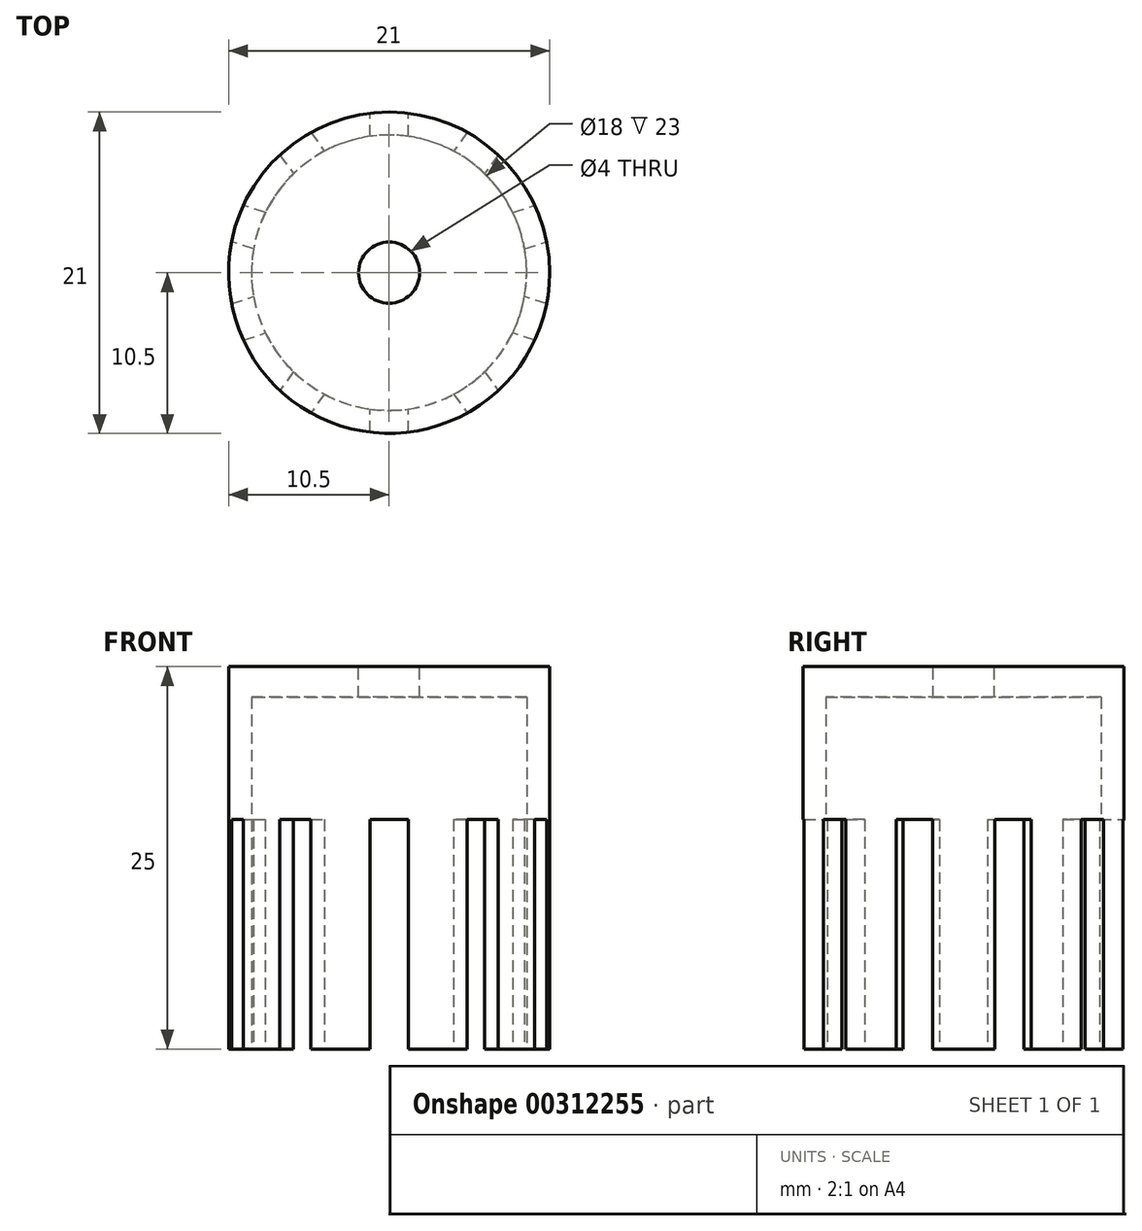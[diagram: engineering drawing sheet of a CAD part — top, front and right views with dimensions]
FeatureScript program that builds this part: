
annotation { "Feature Type Name" : "Feature", "Feature Type Description" : "" }
export const myFeature = defineFeature(function(context is Context, id is Id, definition is map)
    precondition{}
    {
        {
            var Q0;
            Q0=qCreatedBy(makeId("Top.planeOp"),FACE);
            var sketch = newSketch(context, id + "F0", { "sketchPlane" : qUnion([Q0])});
            skCircle(sketch, "E0", {"center": v(0, 0) * mm, "radius": 9 * mm});
            skCircle(sketch, "E1", {"center": v(0, 0) * mm, "radius": 10.5 * mm});
            skSolve(sketch);
        }
        {
            var Q0;
            Q0=makeQuery(id+"F0.imprint","IMPRINT",FACE,{"disambiguationData":[TD([[makeQuery(id+"F0.imprint","IMPRINT",EDGE,{"derivedFrom":sQuery(id+"F0.wireOp",EDGE,"E0")}),-1.0]])]});
            var Q1;
            Q1=makeQuery(id+"F0.imprint","IMPRINT",FACE,{"disambiguationData":[TD([[makeQuery(id+"F0.imprint","IMPRINT",EDGE,{"derivedFrom":sQuery(id+"F0.wireOp",EDGE,"E0")}),1.0]])]});
            extrude(context, id + "F1", {"entities" : qUnion([Q0, Q1]), "depth" : 25 * mm});
        }
        {
            var Q0;
            Q0=makeQuery(id+"F0.imprint","IMPRINT",FACE,{"disambiguationData":[TD([[makeQuery(id+"F0.imprint","IMPRINT",EDGE,{"derivedFrom":sQuery(id+"F0.wireOp",EDGE,"E0")}),1.0]])]});
            extrude(context, id + "F2", {"entities" : qUnion([Q0]), "operationType" : NewBodyOperationType.REMOVE, "depth" : 23 * mm});
        }
        {
            var Q0;
            Q0=makeQuery(id+"F1.opExtrude","CAP_FACE",FACE,{"disambiguationData":[OSD([sQuery(id+"F0.wireOp",EDGE,"E1")])],"isStart":false});
            var sketch = newSketch(context, id + "F3", { "sketchPlane" : qUnion([Q0])});
            skCircle(sketch, "E2", {"center": v(0, 0) * mm, "radius": 2 * mm});
            skSolve(sketch);
        }
        {
            var Q0;
            Q0=makeQuery(id+"F3.imprint","IMPRINT",FACE,{"disambiguationData":[TD([[makeQuery(id+"F3.imprint","IMPRINT",EDGE,{"derivedFrom":sQuery(id+"F3.wireOp",EDGE,"E2")}),1.0]])]});
            extrude(context, id + "F4", {"entities" : qUnion([Q0]), "operationType" : NewBodyOperationType.REMOVE, "endBound" : BoundingType.THROUGH_ALL, "oppositeDirection" : true, "depth" : 25 * mm});
        }
        {
            var Q0;
            Q0=makeQuery(id+"F0.imprint","IMPRINT",FACE,{"disambiguationData":[TD([[makeQuery(id+"F0.imprint","IMPRINT",EDGE,{"derivedFrom":sQuery(id+"F0.wireOp",EDGE,"E0")}),-1.0]])]});
            var sketch = newSketch(context, id + "F5", { "sketchPlane" : qUnion([Q0])});
            skLineSegment(sketch, "E3.bottom", {"start": v(-1.25, -16.71) * mm, "end": v(1.25, -16.71) * mm});
            skLineSegment(sketch, "E3.top", {"start": v(-1.25, 16.71) * mm, "end": v(1.25, 16.71) * mm});
            skLineSegment(sketch, "E3.left", {"start": v(-1.25, -16.71) * mm, "end": v(-1.25, 16.71) * mm});
            skLineSegment(sketch, "E3.right", {"start": v(1.25, -16.71) * mm, "end": v(1.25, 16.71) * mm});
            skLineSegment(sketch, "E4.1.0", {"start": v(15.5, -6.35) * mm, "end": v(-16.28, 3.98) * mm});
            skLineSegment(sketch, "E4.1.1", {"start": v(16.28, -3.98) * mm, "end": v(-15.5, 6.35) * mm});
            skLineSegment(sketch, "E4.1.2", {"start": v(15.5, -6.35) * mm, "end": v(16.28, -3.98) * mm});
            skLineSegment(sketch, "E4.1.3", {"start": v(-16.28, 3.98) * mm, "end": v(-15.5, 6.35) * mm});
            skLineSegment(sketch, "E4.2.0", {"start": v(10.83, 12.78) * mm, "end": v(-8.81, -14.25) * mm});
            skLineSegment(sketch, "E4.2.1", {"start": v(8.81, 14.25) * mm, "end": v(-10.83, -12.78) * mm});
            skLineSegment(sketch, "E4.2.2", {"start": v(10.83, 12.78) * mm, "end": v(8.81, 14.25) * mm});
            skLineSegment(sketch, "E4.2.3", {"start": v(-8.81, -14.25) * mm, "end": v(-10.83, -12.78) * mm});
            skLineSegment(sketch, "E4.3.0", {"start": v(-8.81, 14.25) * mm, "end": v(10.83, -12.78) * mm});
            skLineSegment(sketch, "E4.3.1", {"start": v(-10.83, 12.78) * mm, "end": v(8.81, -14.25) * mm});
            skLineSegment(sketch, "E4.3.2", {"start": v(-8.81, 14.25) * mm, "end": v(-10.83, 12.78) * mm});
            skLineSegment(sketch, "E4.3.3", {"start": v(10.83, -12.78) * mm, "end": v(8.81, -14.25) * mm});
            skLineSegment(sketch, "E4.4.0", {"start": v(-16.28, -3.98) * mm, "end": v(15.5, 6.35) * mm});
            skLineSegment(sketch, "E4.4.1", {"start": v(-15.5, -6.35) * mm, "end": v(16.28, 3.98) * mm});
            skLineSegment(sketch, "E4.4.2", {"start": v(-16.28, -3.98) * mm, "end": v(-15.5, -6.35) * mm});
            skLineSegment(sketch, "E4.4.3", {"start": v(15.5, 6.35) * mm, "end": v(16.28, 3.98) * mm});
            skPoint(sketch, "E4.center", {"position": v(0, 0) * mm});
            skSolve(sketch);
        }
        {
            var Q0;
            {var subQ0=sQuery(id+"F5.wireOp",EDGE,"E4.2.0");var subQ1=makeQuery(id+"F0.imprint","IMPRINT",EDGE,{"derivedFrom":sQuery(id+"F0.wireOp",EDGE,"E1")});var subQ2=makeQuery(id+"F5.imprint","INTERSECT",VERTEX,{"disambiguationData":[OD(0.0)],"derivedFrom":[subQ1,subQ0]});Q0=makeQuery(id+"F5.imprint","IMPRINT",FACE,{"disambiguationData":[TD([[makeQuery(id+"F5.imprint","IMPRINT",EDGE,{"disambiguationData":[TD([[subQ2,-1.0]])],"derivedFrom":subQ0}),-1.0]])]});}
            var Q1;
            {var subQ0=sQuery(id+"F5.wireOp",EDGE,"E4.4.0");var subQ1=makeQuery(id+"F0.imprint","IMPRINT",EDGE,{"derivedFrom":sQuery(id+"F0.wireOp",EDGE,"E1")});var subQ2=makeQuery(id+"F5.imprint","INTERSECT",VERTEX,{"disambiguationData":[OD(1.0)],"derivedFrom":[subQ1,subQ0]});Q1=makeQuery(id+"F5.imprint","IMPRINT",FACE,{"disambiguationData":[TD([[makeQuery(id+"F5.imprint","IMPRINT",EDGE,{"disambiguationData":[TD([[subQ2,1.0]])],"derivedFrom":subQ0}),-1.0]])]});}
            var Q2;
            {var subQ0=sQuery(id+"F5.wireOp",EDGE,"E3.left");var subQ1=makeQuery(id+"F0.imprint","IMPRINT",EDGE,{"derivedFrom":sQuery(id+"F0.wireOp",EDGE,"E1")});var subQ2=makeQuery(id+"F5.imprint","INTERSECT",VERTEX,{"disambiguationData":[OD(1.0)],"derivedFrom":[subQ1,subQ0]});Q2=makeQuery(id+"F5.imprint","IMPRINT",FACE,{"disambiguationData":[TD([[makeQuery(id+"F5.imprint","IMPRINT",EDGE,{"disambiguationData":[TD([[subQ2,1.0]])],"derivedFrom":subQ0}),-1.0]])]});}
            var Q3;
            {var subQ0=sQuery(id+"F5.wireOp",EDGE,"E4.3.0");var subQ1=makeQuery(id+"F0.imprint","IMPRINT",EDGE,{"derivedFrom":sQuery(id+"F0.wireOp",EDGE,"E1")});var subQ2=makeQuery(id+"F5.imprint","INTERSECT",VERTEX,{"disambiguationData":[OD(0.0)],"derivedFrom":[subQ1,subQ0]});Q3=makeQuery(id+"F5.imprint","IMPRINT",FACE,{"disambiguationData":[TD([[makeQuery(id+"F5.imprint","IMPRINT",EDGE,{"disambiguationData":[TD([[subQ2,-1.0]])],"derivedFrom":subQ0}),-1.0]])]});}
            var Q4;
            {var subQ0=sQuery(id+"F5.wireOp",EDGE,"E4.4.0");var subQ1=makeQuery(id+"F0.imprint","IMPRINT",EDGE,{"derivedFrom":sQuery(id+"F0.wireOp",EDGE,"E1")});var subQ2=makeQuery(id+"F5.imprint","INTERSECT",VERTEX,{"disambiguationData":[OD(0.0)],"derivedFrom":[subQ1,subQ0]});Q4=makeQuery(id+"F5.imprint","IMPRINT",FACE,{"disambiguationData":[TD([[makeQuery(id+"F5.imprint","IMPRINT",EDGE,{"disambiguationData":[TD([[subQ2,-1.0]])],"derivedFrom":subQ0}),-1.0]])]});}
            var Q5;
            {var subQ0=sQuery(id+"F5.wireOp",EDGE,"E4.2.0");var subQ1=makeQuery(id+"F0.imprint","IMPRINT",EDGE,{"derivedFrom":sQuery(id+"F0.wireOp",EDGE,"E1")});var subQ2=makeQuery(id+"F5.imprint","INTERSECT",VERTEX,{"disambiguationData":[OD(1.0)],"derivedFrom":[subQ1,subQ0]});Q5=makeQuery(id+"F5.imprint","IMPRINT",FACE,{"disambiguationData":[TD([[makeQuery(id+"F5.imprint","IMPRINT",EDGE,{"disambiguationData":[TD([[subQ2,1.0]])],"derivedFrom":subQ0}),-1.0]])]});}
            var Q6;
            {var subQ0=sQuery(id+"F5.wireOp",EDGE,"E3.left");var subQ1=makeQuery(id+"F0.imprint","IMPRINT",EDGE,{"derivedFrom":sQuery(id+"F0.wireOp",EDGE,"E1")});var subQ2=makeQuery(id+"F5.imprint","INTERSECT",VERTEX,{"disambiguationData":[OD(0.0)],"derivedFrom":[subQ1,subQ0]});Q6=makeQuery(id+"F5.imprint","IMPRINT",FACE,{"disambiguationData":[TD([[makeQuery(id+"F5.imprint","IMPRINT",EDGE,{"disambiguationData":[TD([[subQ2,-1.0]])],"derivedFrom":subQ0}),-1.0]])]});}
            var Q7;
            {var subQ0=sQuery(id+"F5.wireOp",EDGE,"E4.3.0");var subQ1=makeQuery(id+"F0.imprint","IMPRINT",EDGE,{"derivedFrom":sQuery(id+"F0.wireOp",EDGE,"E1")});var subQ2=makeQuery(id+"F5.imprint","INTERSECT",VERTEX,{"disambiguationData":[OD(1.0)],"derivedFrom":[subQ1,subQ0]});Q7=makeQuery(id+"F5.imprint","IMPRINT",FACE,{"disambiguationData":[TD([[makeQuery(id+"F5.imprint","IMPRINT",EDGE,{"disambiguationData":[TD([[subQ2,1.0]])],"derivedFrom":subQ0}),-1.0]])]});}
            var Q8;
            {var subQ0=sQuery(id+"F5.wireOp",EDGE,"E4.1.0");var subQ1=makeQuery(id+"F0.imprint","IMPRINT",EDGE,{"derivedFrom":sQuery(id+"F0.wireOp",EDGE,"E1")});var subQ2=makeQuery(id+"F5.imprint","INTERSECT",VERTEX,{"disambiguationData":[OD(1.0)],"derivedFrom":[subQ1,subQ0]});Q8=makeQuery(id+"F5.imprint","IMPRINT",FACE,{"disambiguationData":[TD([[makeQuery(id+"F5.imprint","IMPRINT",EDGE,{"disambiguationData":[TD([[subQ2,1.0]])],"derivedFrom":subQ0}),-1.0]])]});}
            var Q9;
            {var subQ0=sQuery(id+"F5.wireOp",EDGE,"E4.4.1");var subQ1=sQuery(id+"F5.wireOp",EDGE,"E4.1.0");var subQ2=makeQuery(id+"F5.imprint","INTERSECT",VERTEX,{"derivedFrom":[subQ1,subQ0]});Q9=makeQuery(id+"F5.imprint","IMPRINT",FACE,{"disambiguationData":[TD([[makeQuery(id+"F5.imprint","IMPRINT",EDGE,{"disambiguationData":[TD([[subQ2,-1.0]])],"derivedFrom":subQ1}),1.0]])]});}
            var Q10;
            {var subQ0=sQuery(id+"F5.wireOp",EDGE,"E4.2.0");var subQ1=sQuery(id+"F5.wireOp",EDGE,"E4.1.0");var subQ2=makeQuery(id+"F5.imprint","INTERSECT",VERTEX,{"derivedFrom":[subQ1,subQ0]});Q10=makeQuery(id+"F5.imprint","IMPRINT",FACE,{"disambiguationData":[TD([[makeQuery(id+"F5.imprint","IMPRINT",EDGE,{"disambiguationData":[TD([[subQ2,-1.0]])],"derivedFrom":subQ1}),-1.0]])]});}
            var Q11;
            {var subQ0=sQuery(id+"F5.wireOp",EDGE,"E4.1.0");var subQ1=makeQuery(id+"F0.imprint","IMPRINT",EDGE,{"derivedFrom":sQuery(id+"F0.wireOp",EDGE,"E1")});var subQ2=makeQuery(id+"F5.imprint","INTERSECT",VERTEX,{"disambiguationData":[OD(0.0)],"derivedFrom":[subQ1,subQ0]});Q11=makeQuery(id+"F5.imprint","IMPRINT",FACE,{"disambiguationData":[TD([[makeQuery(id+"F5.imprint","IMPRINT",EDGE,{"disambiguationData":[TD([[subQ2,-1.0]])],"derivedFrom":subQ0}),-1.0]])]});}
            extrude(context, id + "F6", {"entities" : qUnion([Q0, Q1, Q2, Q3, Q4, Q5, Q6, Q7, Q8, Q9, Q10, Q11]), "operationType" : NewBodyOperationType.REMOVE, "depth" : 15 * mm});
        }
    });
